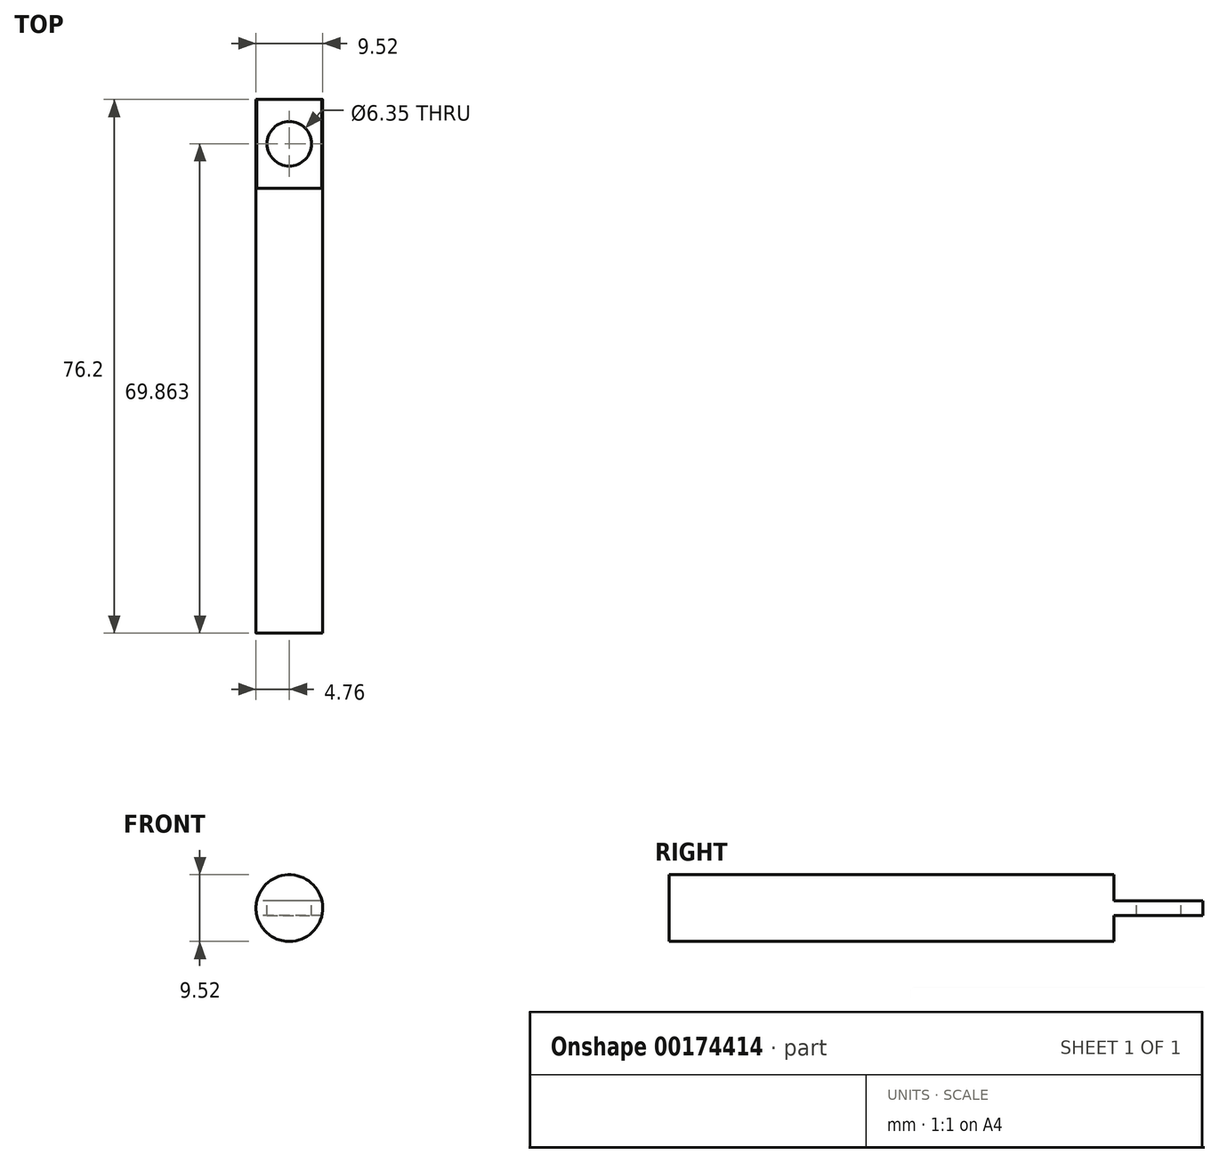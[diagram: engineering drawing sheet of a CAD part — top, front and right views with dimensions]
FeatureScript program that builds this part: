
annotation { "Feature Type Name" : "Feature", "Feature Type Description" : "" }
export const myFeature = defineFeature(function(context is Context, id is Id, definition is map)
    precondition{}
    {
        {
            var Q0;
            Q0=qCreatedBy(makeId("Front.planeOp"),FACE);
            var sketch = newSketch(context, id + "F0", { "sketchPlane" : qUnion([Q0])});
            skCircle(sketch, "E0", {"center": v(0, 0) * mm, "radius": 4.76 * mm});
            skSolve(sketch);
        }
        {
            var Q0;
            Q0 = qSketchRegion(id + "F0", true);
            extrude(context, id + "F1", {"entities" : qUnion([Q0]), "depth" : 76.2 * mm, "offsetDistance" : 25.4 * mm});
        }
        {
            var Q0;
            Q0=makeQuery(id+"F1.opExtrude","CAP_FACE",FACE,{"disambiguationData":[OSD([sQuery(id+"F0.wireOp",EDGE,"E0")])],"isStart":true});
            var sketch = newSketch(context, id + "F2", { "sketchPlane" : qUnion([Q0])});
            skCircle(sketch, "E1", {"center": v(0, 0) * mm, "radius": 4.76 * mm});
            skLineSegment(sketch, "E2", {"start": v(-4.64, 1.07) * mm, "end": v(4.64, 1.07) * mm});
            skLineSegment(sketch, "E3", {"start": v(-4.64, -1.07) * mm, "end": v(4.64, -1.07) * mm});
            skSolve(sketch);
        }
        {
            var Q0;
            {var subQ0=sQuery(id+"F2.wireOp",EDGE,"E2");Q0=makeQuery(id+"F2.imprint","IMPRINT",FACE,{"disambiguationData":[TD([[makeQuery(id+"F2.imprint","IMPRINT",EDGE,{"derivedFrom":subQ0}),1.0]])]});}
            var Q1;
            {var subQ0=sQuery(id+"F2.wireOp",EDGE,"E3");Q1=makeQuery(id+"F2.imprint","IMPRINT",FACE,{"disambiguationData":[TD([[makeQuery(id+"F2.imprint","IMPRINT",EDGE,{"derivedFrom":subQ0}),-1.0]])]});}
            extrude(context, id + "F3", {"entities" : qUnion([Q0, Q1]), "operationType" : NewBodyOperationType.REMOVE, "oppositeDirection" : true, "depth" : 12.7 * mm, "offsetDistance" : 25.4 * mm});
        }
        {
            var Q0;
            Q0=makeQuery(id+"F3.boolean.opBoolean","COPY",FACE,{"derivedFrom":makeQuery(id+"F3.opExtrude","SWEPT_FACE",FACE,{"disambiguationData":[OSD([sQuery(id+"F2.wireOp",EDGE,"E2")])]})});
            var sketch = newSketch(context, id + "F4", { "sketchPlane" : qUnion([Q0])});
            skCircle(sketch, "E4", {"center": v(0, -6.34) * mm, "radius": 3.18 * mm});
            skSolve(sketch);
        }
        {
            var Q0;
            Q0 = qSketchRegion(id + "F4", true);
            extrude(context, id + "F5", {"entities" : qUnion([Q0]), "operationType" : NewBodyOperationType.REMOVE, "oppositeDirection" : true, "depth" : 25.4 * mm, "offsetDistance" : 25.4 * mm});
        }
    });
